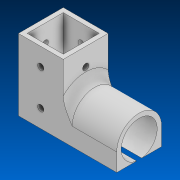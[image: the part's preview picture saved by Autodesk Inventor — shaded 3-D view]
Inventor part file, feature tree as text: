
AUTODESK INVENTOR PART (.ipt)
format: ipt  version: 2022 (Build 260153000, 153)  size: 160,768 bytes
history: native  units: in
note: dims shown in document units (in); Inventor stores cm internally (conversion verified against a paired STEP export)
features: sketch x4, extrude x3, hole x2, fillet x1
ambient origin geometry x8: Origin, YZ Plane, XZ Plane, XY Plane, X Axis, Y Axis, Z Axis, Center Point
bodies: Solid1 (feature_tree)
feature tree (10):
  extrude  "Extrusion1"  Depth=1.01in
  hole  "Hole1"  [1 undecoded]
  hole  "Hole2"  [1 undecoded]
  sketch  "Sketch4"  dims[d7=0.175in d8=0.75in d9=0.375in d10=0.25in d11=0.5635in d12=1.0in d13=0.8108in d14=0.175in d15=0.75in d16=0.375in d17=0.25in d18=0.5635in d19=1.0in d20=0.8108in d21=1.5in d22=0.0in d23=2.0in d24=0.0in d25=0.25in d26=1.0in d27=1.01in d28=0.5in d29=0.0344in d30=0.5in d31=0.0344in]
  extrude  "Extrusion2"  Depth=0.25in TaperAngle=0.0deg
  extrude  "Extrusion3"  Depth=0.25in TaperAngle=0.0deg
  fillet  "Fillet1"  Radius=0.25in
  sketch  "Sketch1"  dims[d0=1.01in d1=1.01in]
  sketch  "Sketch2"  dims[d2=0.125in d3=2.0in d4=0.0in]
  sketch  "Sketch3"  dims[d5=0.5in d6=1.0in]
note: 2 required parameter values undecoded (feature->parameter linkage not recoverable at this tier; creation-order binding heuristic only, values carry confidence <= 0.55)
